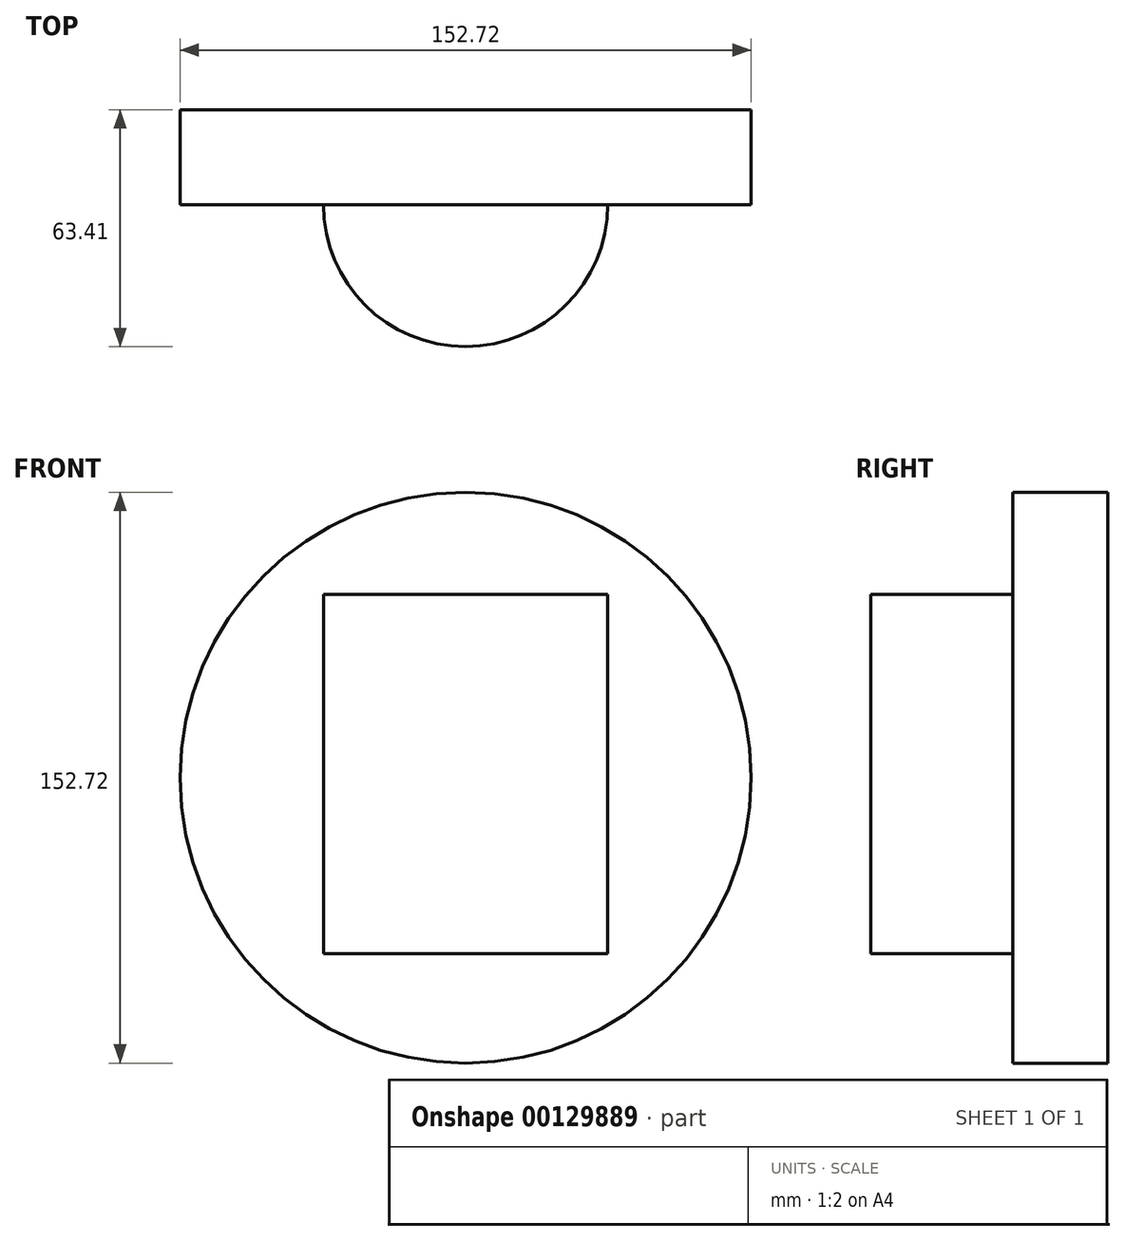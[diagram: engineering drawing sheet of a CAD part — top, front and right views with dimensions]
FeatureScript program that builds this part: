
annotation { "Feature Type Name" : "Feature", "Feature Type Description" : "" }
export const myFeature = defineFeature(function(context is Context, id is Id, definition is map)
    precondition{}
    {
        {
            var Q0;
            Q0=qCreatedBy(makeId("Front.planeOp"),FACE);
            var sketch = newSketch(context, id + "F0", { "sketchPlane" : qUnion([Q0])});
            skCircle(sketch, "E0", {"center": v(0, 0) * mm, "radius": 76.36 * mm});
            skSolve(sketch);
        }
        {
            var Q0;
            Q0=makeQuery(id+"F0.imprint","IMPRINT",FACE,{"disambiguationData":[TD([[makeQuery(id+"F0.imprint","IMPRINT",EDGE,{"derivedFrom":sQuery(id+"F0.wireOp",EDGE,"E0")}),1.0]])]});
            extrude(context, id + "F1", {"entities" : qUnion([Q0]), "depth" : 25.4 * mm});
        }
        {
            var Q0;
            Q0=makeQuery(id+"F1.opExtrude","CAP_FACE",FACE,{"disambiguationData":[OSD([sQuery(id+"F0.wireOp",EDGE,"E0")])],"isStart":false});
            var sketch = newSketch(context, id + "F2", { "sketchPlane" : qUnion([Q0])});
            skLineSegment(sketch, "E1.bottom", {"start": v(0, 49.04) * mm, "end": v(38, 49.04) * mm});
            skLineSegment(sketch, "E1.top", {"start": v(0, -47.07) * mm, "end": v(38, -47.07) * mm});
            skLineSegment(sketch, "E1.left", {"start": v(0, 49.04) * mm, "end": v(0, -47.07) * mm});
            skLineSegment(sketch, "E1.right", {"start": v(38, 49.04) * mm, "end": v(38, -47.07) * mm});
            skSolve(sketch);
        }
        {
            var Q0;
            Q0=makeQuery(id+"F2.imprint","IMPRINT",FACE,{"disambiguationData":[TD([[makeQuery(id+"F2.imprint","IMPRINT",EDGE,{"derivedFrom":sQuery(id+"F2.wireOp",EDGE,"E1.bottom")}),-1.0]])]});
            var Q1;
            Q1=sQuery(id+"F2.wireOp",EDGE,"E1.left");
            revolve(context, id + "F3", {"operationType" : NewBodyOperationType.ADD, "entities" : qUnion([Q0]), "axis" : qUnion([Q1]), "revolveType" : RevolveType.ONE_DIRECTION, "angle" : 180 * degree});
        }
    });
